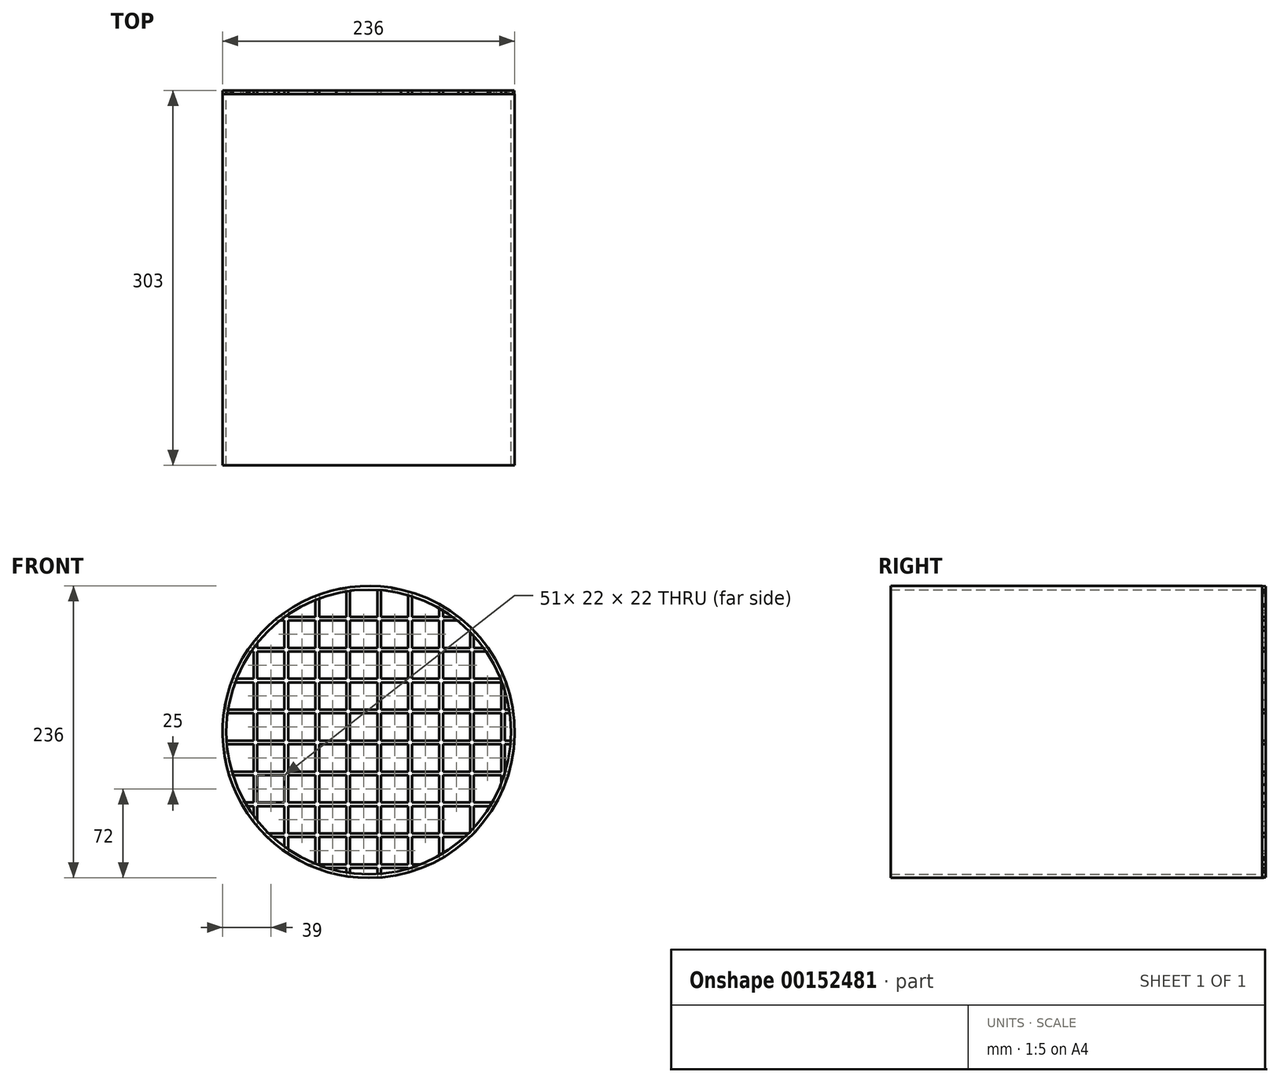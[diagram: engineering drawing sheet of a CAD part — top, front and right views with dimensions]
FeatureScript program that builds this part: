
annotation { "Feature Type Name" : "Feature", "Feature Type Description" : "" }
export const myFeature = defineFeature(function(context is Context, id is Id, definition is map)
    precondition{}
    {
        {
            var Q0;
            Q0=qCreatedBy(makeId("Front.planeOp"),FACE);
            var sketch = newSketch(context, id + "F0", { "sketchPlane" : qUnion([Q0])});
            skCircle(sketch, "E0", {"center": v(0, 0) * mm, "radius": 115 * mm});
            skCircle(sketch, "E1", {"center": v(0, 0) * mm, "radius": 118 * mm});
            skSolve(sketch);
        }
        {
            var Q0;
            Q0=makeQuery(id+"F0.imprint","IMPRINT",FACE,{"disambiguationData":[TD([[makeQuery(id+"F0.imprint","IMPRINT",EDGE,{"derivedFrom":sQuery(id+"F0.wireOp",EDGE,"E0")}),-1.0]])]});
            extrude(context, id + "F1", {"entities" : qUnion([Q0]), "depth" : 300 * mm});
        }
        {
            var Q0;
            Q0=qCreatedBy(makeId("Front.planeOp"),FACE);
            var sketch = newSketch(context, id + "F2", { "sketchPlane" : qUnion([Q0])});
            skLineSegment(sketch, "E2.bottom", {"start": v(-118, 118) * mm, "end": v(-115, 118) * mm});
            skLineSegment(sketch, "E2.top", {"start": v(-118, -118) * mm, "end": v(-115, -118) * mm});
            skLineSegment(sketch, "E2.left", {"start": v(-118, 118) * mm, "end": v(-118, -118) * mm});
            skLineSegment(sketch, "E2.right", {"start": v(-115, 118) * mm, "end": v(-115, -118) * mm});
            skLineSegment(sketch, "E3.1.0.0", {"start": v(-90, 118) * mm, "end": v(-90, -118) * mm});
            skLineSegment(sketch, "E3.1.0.1", {"start": v(-93, 118) * mm, "end": v(-93, -118) * mm});
            skLineSegment(sketch, "E3.1.0.2", {"start": v(-93, -118) * mm, "end": v(-90, -118) * mm});
            skLineSegment(sketch, "E3.1.0.3", {"start": v(-93, 118) * mm, "end": v(-90, 118) * mm});
            skLineSegment(sketch, "E3.2.0.0", {"start": v(-65, 118) * mm, "end": v(-65, -118) * mm});
            skLineSegment(sketch, "E3.2.0.1", {"start": v(-68, 118) * mm, "end": v(-68, -118) * mm});
            skLineSegment(sketch, "E3.2.0.2", {"start": v(-68, -118) * mm, "end": v(-65, -118) * mm});
            skLineSegment(sketch, "E3.2.0.3", {"start": v(-68, 118) * mm, "end": v(-65, 118) * mm});
            skLineSegment(sketch, "E3.3.0.0", {"start": v(-40, 118) * mm, "end": v(-40, -118) * mm});
            skLineSegment(sketch, "E3.3.0.1", {"start": v(-43, 118) * mm, "end": v(-43, -118) * mm});
            skLineSegment(sketch, "E3.3.0.2", {"start": v(-43, -118) * mm, "end": v(-40, -118) * mm});
            skLineSegment(sketch, "E3.3.0.3", {"start": v(-43, 118) * mm, "end": v(-40, 118) * mm});
            skLineSegment(sketch, "E3.4.0.0", {"start": v(-15, 118) * mm, "end": v(-15, -118) * mm});
            skLineSegment(sketch, "E3.4.0.1", {"start": v(-18, 118) * mm, "end": v(-18, -118) * mm});
            skLineSegment(sketch, "E3.4.0.2", {"start": v(-18, -118) * mm, "end": v(-15, -118) * mm});
            skLineSegment(sketch, "E3.4.0.3", {"start": v(-18, 118) * mm, "end": v(-15, 118) * mm});
            skLineSegment(sketch, "E3.5.0.0", {"start": v(10, 118) * mm, "end": v(10, -118) * mm});
            skLineSegment(sketch, "E3.5.0.1", {"start": v(7, 118) * mm, "end": v(7, -118) * mm});
            skLineSegment(sketch, "E3.5.0.2", {"start": v(7, -118) * mm, "end": v(10, -118) * mm});
            skLineSegment(sketch, "E3.5.0.3", {"start": v(7, 118) * mm, "end": v(10, 118) * mm});
            skLineSegment(sketch, "E3.6.0.0", {"start": v(35, 118) * mm, "end": v(35, -118) * mm});
            skLineSegment(sketch, "E3.6.0.1", {"start": v(32, 118) * mm, "end": v(32, -118) * mm});
            skLineSegment(sketch, "E3.6.0.2", {"start": v(32, -118) * mm, "end": v(35, -118) * mm});
            skLineSegment(sketch, "E3.6.0.3", {"start": v(32, 118) * mm, "end": v(35, 118) * mm});
            skLineSegment(sketch, "E3.7.0.0", {"start": v(60, 118) * mm, "end": v(60, -118) * mm});
            skLineSegment(sketch, "E3.7.0.1", {"start": v(57, 118) * mm, "end": v(57, -118) * mm});
            skLineSegment(sketch, "E3.7.0.2", {"start": v(57, -118) * mm, "end": v(60, -118) * mm});
            skLineSegment(sketch, "E3.7.0.3", {"start": v(57, 118) * mm, "end": v(60, 118) * mm});
            skLineSegment(sketch, "E3.8.0.0", {"start": v(85, 118) * mm, "end": v(85, -118) * mm});
            skLineSegment(sketch, "E3.8.0.1", {"start": v(82, 118) * mm, "end": v(82, -118) * mm});
            skLineSegment(sketch, "E3.8.0.2", {"start": v(82, -118) * mm, "end": v(85, -118) * mm});
            skLineSegment(sketch, "E3.8.0.3", {"start": v(82, 118) * mm, "end": v(85, 118) * mm});
            skLineSegment(sketch, "E3.9.0.0", {"start": v(110, 118) * mm, "end": v(110, -118) * mm});
            skLineSegment(sketch, "E3.9.0.1", {"start": v(107, 118) * mm, "end": v(107, -118) * mm});
            skLineSegment(sketch, "E3.9.0.2", {"start": v(107, -118) * mm, "end": v(110, -118) * mm});
            skLineSegment(sketch, "E3.9.0.3", {"start": v(107, 118) * mm, "end": v(110, 118) * mm});
            skLineSegment(sketch, "E3.10.0.0", {"start": v(135, 118) * mm, "end": v(135, -118) * mm});
            skLineSegment(sketch, "E3.10.0.1", {"start": v(132, 118) * mm, "end": v(132, -118) * mm});
            skLineSegment(sketch, "E3.10.0.2", {"start": v(132, -118) * mm, "end": v(135, -118) * mm});
            skLineSegment(sketch, "E3.10.0.3", {"start": v(132, 118) * mm, "end": v(135, 118) * mm});
            skLineSegment(sketch, "E3.11.0.0", {"start": v(160, 118) * mm, "end": v(160, -118) * mm});
            skLineSegment(sketch, "E3.11.0.1", {"start": v(157, 118) * mm, "end": v(157, -118) * mm});
            skLineSegment(sketch, "E3.11.0.2", {"start": v(157, -118) * mm, "end": v(160, -118) * mm});
            skLineSegment(sketch, "E3.11.0.3", {"start": v(157, 118) * mm, "end": v(160, 118) * mm});
            skLineSegment(sketch, "E3.12.0.0", {"start": v(185, 118) * mm, "end": v(185, -118) * mm});
            skLineSegment(sketch, "E3.12.0.1", {"start": v(182, 118) * mm, "end": v(182, -118) * mm});
            skLineSegment(sketch, "E3.12.0.2", {"start": v(182, -118) * mm, "end": v(185, -118) * mm});
            skLineSegment(sketch, "E3.12.0.3", {"start": v(182, 118) * mm, "end": v(185, 118) * mm});
            skLineSegment(sketch, "E3.direction1", {"start": v(-115, -118) * mm, "end": v(-90, -118) * mm, "construction": true});
            skSolve(sketch);
        }
        {
            var Q0;
            Q0=qSketchRegion(id+"F2",true);
            extrude(context, id + "F3", {"entities" : qUnion([Q0]), "operationType" : NewBodyOperationType.ADD, "oppositeDirection" : true, "depth" : 3 * mm});
        }
        {
            var Q0;
            Q0=qCreatedBy(makeId("Front.planeOp"),FACE);
            var sketch = newSketch(context, id + "F4", { "sketchPlane" : qUnion([Q0])});
            skLineSegment(sketch, "E4.bottom", {"start": v(118, 118) * mm, "end": v(-118, 118) * mm});
            skLineSegment(sketch, "E4.top", {"start": v(118, 115) * mm, "end": v(-118, 115) * mm});
            skLineSegment(sketch, "E4.left", {"start": v(118, 118) * mm, "end": v(118, 115) * mm});
            skLineSegment(sketch, "E4.right", {"start": v(-118, 118) * mm, "end": v(-118, 115) * mm});
            skLineSegment(sketch, "E5.1.0.0", {"start": v(118, 93) * mm, "end": v(-118, 93) * mm});
            skLineSegment(sketch, "E5.1.0.1", {"start": v(118, 90) * mm, "end": v(-118, 90) * mm});
            skLineSegment(sketch, "E5.1.0.2", {"start": v(118, 93) * mm, "end": v(118, 90) * mm});
            skLineSegment(sketch, "E5.1.0.3", {"start": v(-118, 93) * mm, "end": v(-118, 90) * mm});
            skLineSegment(sketch, "E5.2.0.0", {"start": v(118, 68) * mm, "end": v(-118, 68) * mm});
            skLineSegment(sketch, "E5.2.0.1", {"start": v(118, 65) * mm, "end": v(-118, 65) * mm});
            skLineSegment(sketch, "E5.2.0.2", {"start": v(118, 68) * mm, "end": v(118, 65) * mm});
            skLineSegment(sketch, "E5.2.0.3", {"start": v(-118, 68) * mm, "end": v(-118, 65) * mm});
            skLineSegment(sketch, "E5.3.0.0", {"start": v(118, 43) * mm, "end": v(-118, 43) * mm});
            skLineSegment(sketch, "E5.3.0.1", {"start": v(118, 40) * mm, "end": v(-118, 40) * mm});
            skLineSegment(sketch, "E5.3.0.2", {"start": v(118, 43) * mm, "end": v(118, 40) * mm});
            skLineSegment(sketch, "E5.3.0.3", {"start": v(-118, 43) * mm, "end": v(-118, 40) * mm});
            skLineSegment(sketch, "E5.4.0.0", {"start": v(118, 18) * mm, "end": v(-118, 18) * mm});
            skLineSegment(sketch, "E5.4.0.1", {"start": v(118, 15) * mm, "end": v(-118, 15) * mm});
            skLineSegment(sketch, "E5.4.0.2", {"start": v(118, 18) * mm, "end": v(118, 15) * mm});
            skLineSegment(sketch, "E5.4.0.3", {"start": v(-118, 18) * mm, "end": v(-118, 15) * mm});
            skLineSegment(sketch, "E5.5.0.0", {"start": v(118, -7) * mm, "end": v(-118, -7) * mm});
            skLineSegment(sketch, "E5.5.0.1", {"start": v(118, -10) * mm, "end": v(-118, -10) * mm});
            skLineSegment(sketch, "E5.5.0.2", {"start": v(118, -7) * mm, "end": v(118, -10) * mm});
            skLineSegment(sketch, "E5.5.0.3", {"start": v(-118, -7) * mm, "end": v(-118, -10) * mm});
            skLineSegment(sketch, "E5.6.0.0", {"start": v(118, -32) * mm, "end": v(-118, -32) * mm});
            skLineSegment(sketch, "E5.6.0.1", {"start": v(118, -35) * mm, "end": v(-118, -35) * mm});
            skLineSegment(sketch, "E5.6.0.2", {"start": v(118, -32) * mm, "end": v(118, -35) * mm});
            skLineSegment(sketch, "E5.6.0.3", {"start": v(-118, -32) * mm, "end": v(-118, -35) * mm});
            skLineSegment(sketch, "E5.7.0.0", {"start": v(118, -57) * mm, "end": v(-118, -57) * mm});
            skLineSegment(sketch, "E5.7.0.1", {"start": v(118, -60) * mm, "end": v(-118, -60) * mm});
            skLineSegment(sketch, "E5.7.0.2", {"start": v(118, -57) * mm, "end": v(118, -60) * mm});
            skLineSegment(sketch, "E5.7.0.3", {"start": v(-118, -57) * mm, "end": v(-118, -60) * mm});
            skLineSegment(sketch, "E5.8.0.0", {"start": v(118, -82) * mm, "end": v(-118, -82) * mm});
            skLineSegment(sketch, "E5.8.0.1", {"start": v(118, -85) * mm, "end": v(-118, -85) * mm});
            skLineSegment(sketch, "E5.8.0.2", {"start": v(118, -82) * mm, "end": v(118, -85) * mm});
            skLineSegment(sketch, "E5.8.0.3", {"start": v(-118, -82) * mm, "end": v(-118, -85) * mm});
            skLineSegment(sketch, "E5.9.0.0", {"start": v(118, -107) * mm, "end": v(-118, -107) * mm});
            skLineSegment(sketch, "E5.9.0.1", {"start": v(118, -110) * mm, "end": v(-118, -110) * mm});
            skLineSegment(sketch, "E5.9.0.2", {"start": v(118, -107) * mm, "end": v(118, -110) * mm});
            skLineSegment(sketch, "E5.9.0.3", {"start": v(-118, -107) * mm, "end": v(-118, -110) * mm});
            skLineSegment(sketch, "E5.10.0.0", {"start": v(118, -132) * mm, "end": v(-118, -132) * mm});
            skLineSegment(sketch, "E5.10.0.1", {"start": v(118, -135) * mm, "end": v(-118, -135) * mm});
            skLineSegment(sketch, "E5.10.0.2", {"start": v(118, -132) * mm, "end": v(118, -135) * mm});
            skLineSegment(sketch, "E5.10.0.3", {"start": v(-118, -132) * mm, "end": v(-118, -135) * mm});
            skLineSegment(sketch, "E5.11.0.0", {"start": v(118, -157) * mm, "end": v(-118, -157) * mm});
            skLineSegment(sketch, "E5.11.0.1", {"start": v(118, -160) * mm, "end": v(-118, -160) * mm});
            skLineSegment(sketch, "E5.11.0.2", {"start": v(118, -157) * mm, "end": v(118, -160) * mm});
            skLineSegment(sketch, "E5.11.0.3", {"start": v(-118, -157) * mm, "end": v(-118, -160) * mm});
            skLineSegment(sketch, "E5.12.0.0", {"start": v(118, -182) * mm, "end": v(-118, -182) * mm});
            skLineSegment(sketch, "E5.12.0.1", {"start": v(118, -185) * mm, "end": v(-118, -185) * mm});
            skLineSegment(sketch, "E5.12.0.2", {"start": v(118, -182) * mm, "end": v(118, -185) * mm});
            skLineSegment(sketch, "E5.12.0.3", {"start": v(-118, -182) * mm, "end": v(-118, -185) * mm});
            skLineSegment(sketch, "E5.direction1", {"start": v(-118, 118) * mm, "end": v(-118, 93) * mm, "construction": true});
            skSolve(sketch);
        }
        {
            var Q0;
            Q0=qSketchRegion(id+"F4",true);
            extrude(context, id + "F5", {"entities" : qUnion([Q0]), "operationType" : NewBodyOperationType.ADD, "oppositeDirection" : true, "depth" : 3 * mm});
        }
        {
            var Q0;
            Q0=qCreatedBy(makeId("Front.planeOp"),FACE);
            var sketch = newSketch(context, id + "F6", { "sketchPlane" : qUnion([Q0])});
            skCircle(sketch, "E6", {"center": v(0, 0) * mm, "radius": 118 * mm});
            skCircle(sketch, "E7", {"center": v(0, 0) * mm, "radius": 233.52 * mm});
            skSolve(sketch);
        }
        {
            var Q0;
            Q0=qSketchRegion(id+"F6",true);
            extrude(context, id + "F7", {"entities" : qUnion([Q0]), "operationType" : NewBodyOperationType.REMOVE, "oppositeDirection" : true, "depth" : 25 * mm, "hasDraft" : true, "draftAngle" : 3 * degree});
        }
    });
